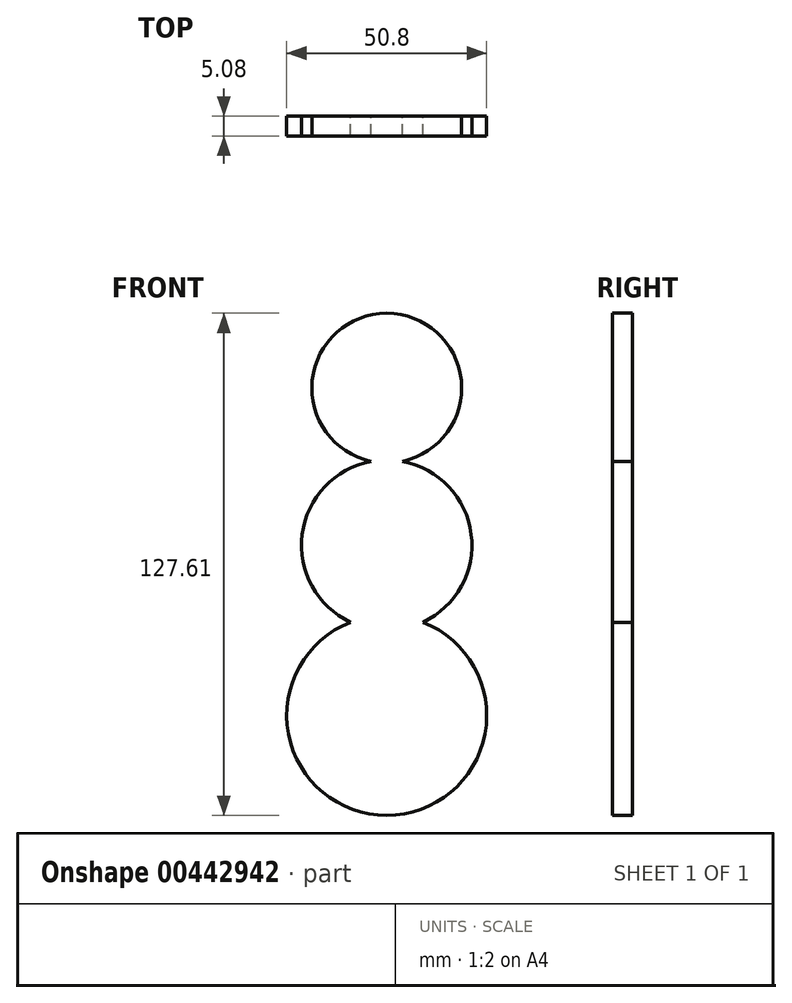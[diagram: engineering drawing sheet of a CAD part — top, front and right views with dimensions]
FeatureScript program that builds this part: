
annotation { "Feature Type Name" : "Feature", "Feature Type Description" : "" }
export const myFeature = defineFeature(function(context is Context, id is Id, definition is map)
    precondition{}
    {
        {
            var Q0;
            Q0=qCreatedBy(makeId("Front.planeOp"),FACE);
            var sketch = newSketch(context, id + "F0", { "sketchPlane" : qUnion([Q0])});
            skCircle(sketch, "E0", {"center": v(0, -35.98) * mm, "radius": 25.4 * mm});
            skCircle(sketch, "E1", {"center": v(0, 7.3) * mm, "radius": 21.64 * mm});
            skCircle(sketch, "E2", {"center": v(0, 47.2) * mm, "radius": 19.03 * mm});
            skSolve(sketch);
        }
        {
            var Q0;
            Q0 = qSketchRegion(id + "F0", true);
            extrude(context, id + "F1", {"entities" : qUnion([Q0]), "depth" : 5.08 * mm});
        }
    });
